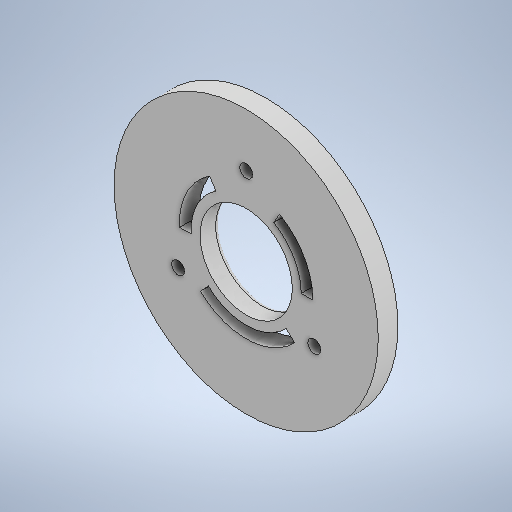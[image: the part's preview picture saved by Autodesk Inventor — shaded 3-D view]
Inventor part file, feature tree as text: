
AUTODESK INVENTOR PART (.ipt)
format: ipt  version: 2025 (Build 290162000, 162)  size: 331,264 bytes
history: native  units: mm
features: sketch x3, extrude x3, fillet x1, chamfer x1
ambient origin geometry x8: Origin, YZ Plane, XZ Plane, XY Plane, X Axis, Y Axis, Z Axis, Center Point
bodies: 实体1 (feature_tree)
feature tree (8):
  sketch  "草图1"  dims[d0=67.2mm d1=40.0mm]
  extrude  "拉伸1"  Depth=40.0mm
  extrude  "拉伸2"  Depth=30.0mm TaperAngle=360.0deg
  extrude  "拉伸3"  Depth=10.0mm TaperAngle=0.0deg
  fillet  "圆角1"  Radius=43.3mm
  chamfer  "倒角1"  Distance=10.0mm
  sketch  "草图 - 环形阵列1"  dims[d2=3.3mm d3=30.0mm d5=360.0deg]
  sketch  "草图 - 环形阵列2"  dims[d7=23.5mm d8=5.0mm d9=0.0mm d10=43.3mm d11=10.0mm d12=160.0mm d14=360.0deg d16=2.0mm d17=0.0mm d18=14.0mm d19=3.0mm d20=45.0deg d21=60.0deg d22=45.0deg d23=5.0mm d24=0.0mm d25=1.0mm d26=1.0mm d27=2.0mm d28=45.0deg]
